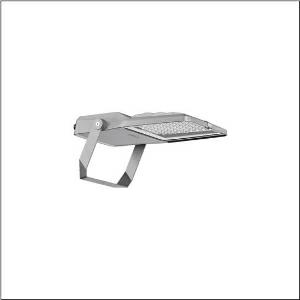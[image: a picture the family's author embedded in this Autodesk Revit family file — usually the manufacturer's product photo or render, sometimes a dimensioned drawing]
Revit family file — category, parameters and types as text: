
# Revit family: floodlight_fl_21_iq_mini___pl64_5xa7771d4e1a_9fb1
name_source: partatom
category: Lighting Fixtures
units: mm (PartAtom-declared; Revit-internal decimal feet)

## family parameters
Cut with Voids When Loaded = No
Host = Face
Light Source = No
Part Type = Normal
Room Calculation Point = No
Round Connector Dimension = Use Diameter
Shared = No

## types (1)
- --- (1 x LED, 17970 lm, 143 W, 4000K)
    Apparent Load = 143 VA
    CIE Flux Codes = 28 80 98 100 100
    Color Rendering = 70
    Color Temperature = 4000K
    Default Elevation = 1800 mm
    Description = Floodlight FL 21 iQ mini, floodlight, primary light control with lens, of PMMA, primary optical cover: protective disc, of toughened safety glass, transparent, light distribution: PL64, light emission: direct distribution, installation type: surface-mounted, lamps: LED, High Power LED, rated values: 17.970lm | 143W | 125,7lm/W (begin service life); end service life: 17.970lm | 151,6W; at 50% lumin. flux: 8.985lm | 60,8W | 147,8lm/W, colour temperature: 4000K, colour rendering: CRI > 70, light colour: 740, light setting 1 begin service life: 100% | 17.970lm | 143W | 125,7lm/W | 4.000K, light setting 1 end service life: 151,6W, further light settings possible, control: Auto-Match, Temp-Guard, Lumen-Switch, Night-Set, Smart-Wire, Light-Fading, Desk-Remote (wireless, voltage-free reading and setting of iQ features in the workshop via application-optimized NFC function/RFID function), optimised constant luminous flux control (CLO 2.0), pre-setting: linear dimming characteristic, with terminal, 6-pole, mains connection: 220..240V, AC, 50/60Hz, luminaire housing, of diecast aluminium, powder-coated, SITECO metallic grey (DB 702S), corrosivity category C5 mid according to DIN EN ISO 12944suitable for swimming poolschlorine-resistant, sealing non-destructively replaceable, mounting bracket, of steel, galvanised, powder-coated, SITECO metallic grey (DB 702S), protection rating (complete): IP66, insulation class (complete): insulation class II (safety insulation), certification: CE, ENEC, VDE, protection symbol: D, impact resistance: IK08, permissible operating ambient temperature: -40..+40°C, permissible operating ambient temperature for outdoor applications: -40..+50°C, standard: DIN EN 12944, LABS conformity tested according to VDMA 24364:2018-05, packaging unit: 1 piece

Light Distribution: PL64
    Height = 70 mm
    Lamp = 1 x LED
    Lamp Light Flux = 17970 lm
    Lamp Power = 143 W
    Lamp count = 1
    Length = 485 mm
    Luminous efficacy = 126 lm/W
    Manufacturer = Siteco
    ModVariant = No
    Model = 5XA7771D4E1A
    Number of Poles = 1
    OnlyDefault = Yes
    Power Factor = 1
    Product Name = Floodlight FL 21 iQ mini | PL64
    Product group = floodlight | pylon annexe
    ProductGroupID = 6201
    Protection Class = Protection class II
    Protection Degree = IP 66
    RLX_Detail_Level = 1
    RLX_Emergency_Light_Flux = 0 lm
    RLX_Emergency_Type = 0
    RLX_Emergency_Type_DB = No
    RlxData = <blob elided: 96869 chars, md5=90281617>
    Socket = socket
    Standby Power = 0 W
    System Light Flux = 17970 lm
    System Power = 143 W
    Type Comments = factory setting: luminous flux: 100 % | dim-lin: 254 | 730 mA
    Type Image = l_1006845.jpg
    URL = http://relux.com
    VarID = @adj_165507
    Voltage = 0 V
    Weight = 0.00 kg
    Width = 337 mm

## geometry (parser evidence)
native form markers: Blend x4, Sweep x12
no freeform markers — native parametric forms only
